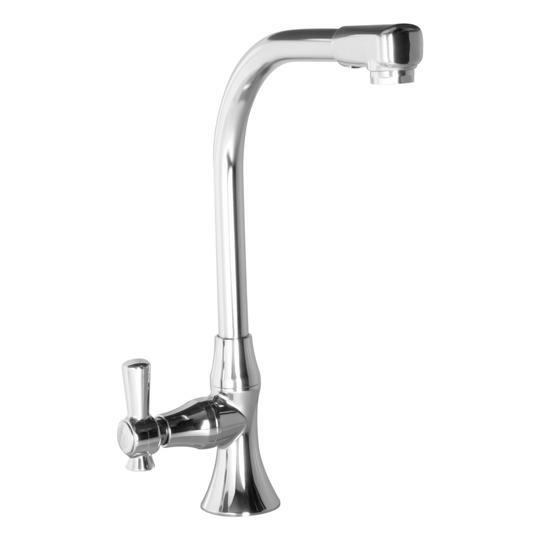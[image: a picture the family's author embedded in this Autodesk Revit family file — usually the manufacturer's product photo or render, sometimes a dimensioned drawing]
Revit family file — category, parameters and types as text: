
# Revit family: 01-1450-11 LLAVE MOVIL LAVAPLATOS TOSCANA
name_source: partatom
category: Plumbing Fixtures
revit_build: Autodesk Revit 2018 (Build: 20170223_1515(x64)
units: mm (PartAtom-declared; Revit-internal decimal feet)

## family parameters
Cut with Voids When Loaded = No
Host = Face
OmniClass Number = 23.31.11.00
Part Type = Normal
Room Calculation Point = No
Round Connector Dimension = Use Diameter
Shared = No

## types (1)
- 01-1450-11
    Alto = 309 mm
    Alto Aireador = 273 mm  [stored 0.895669 ft]
    CW Connection = Yes
    Default Elevation = 0 mm  [stored 0 ft]
    Description = Monomando
    Eje - Aireador = 175 mm
    HW Connection = Yes
    Link Ficha Tecnica = http://infotecnica.gricol.com
    Manija = 70 mm
    Manufacturer = Gricol
    Model = 01-1450-11
    Plastico ABS Cromado = Plastico - ABS Cromado
    Product Name = LLAVE MOVIL LAVAPLATOS TOSCANA
    Type Image = LLAVE MOVIL LAVAPLATOS TOSCANA.jpg
    URL = https://www.gricol.com
    Vent Connection = No
    Waste Connection = No

note: [stored X ft] marks values corroborated as IEEE doubles in the binary element streams (Revit-internal decimal feet)

## geometry (parser evidence)
native form markers: Blend x2, Sweep x2
no freeform markers — native parametric forms only
